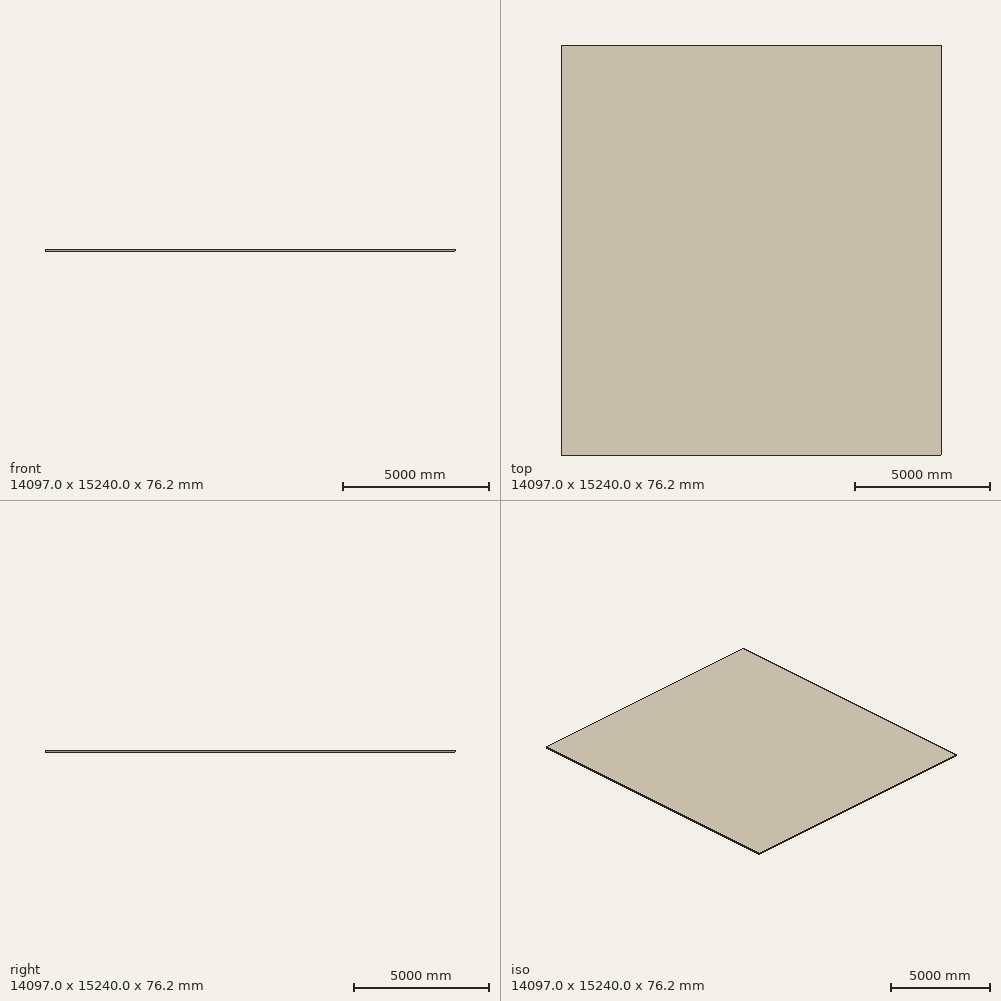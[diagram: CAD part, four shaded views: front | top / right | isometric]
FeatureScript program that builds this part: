
annotation { "Feature Type Name" : "Feature", "Feature Type Description" : "" }
export const myFeature = defineFeature(function(context is Context, id is Id, definition is map)
    precondition{}
    {
        {
            var Q0;
            Q0=qCreatedBy(makeId("Top.planeOp"),FACE);
            var sketch = newSketch(context, id + "F0", { "sketchPlane" : qUnion([Q0])});
            skLineSegment(sketch, "E0.bottom", {"start": v(7048.5, -7620) * mm, "end": v(-7048.5, -7620) * mm});
            skLineSegment(sketch, "E0.top", {"start": v(7048.5, 7620) * mm, "end": v(-7048.5, 7620) * mm});
            skLineSegment(sketch, "E0.left", {"start": v(7048.5, -7620) * mm, "end": v(7048.5, 7620) * mm});
            skLineSegment(sketch, "E0.right", {"start": v(-7048.5, -7620) * mm, "end": v(-7048.5, 7620) * mm});
            skPoint(sketch, "E0.middle", {"position": v(0, 0) * mm});
            skSolve(sketch);
        }
        {
            var Q0;
            Q0=makeQuery(id+"F0.imprint","IMPRINT",FACE,{"disambiguationData":[TD([[makeQuery(id+"F0.imprint","IMPRINT",EDGE,{"derivedFrom":sQuery(id+"F0.wireOp",EDGE,"E0.bottom")}),-1.0]])]});
            extrude(context, id + "F1", {"entities" : qUnion([Q0]), "oppositeDirection" : true, "depth" : 76.2 * mm});
        }
    });
